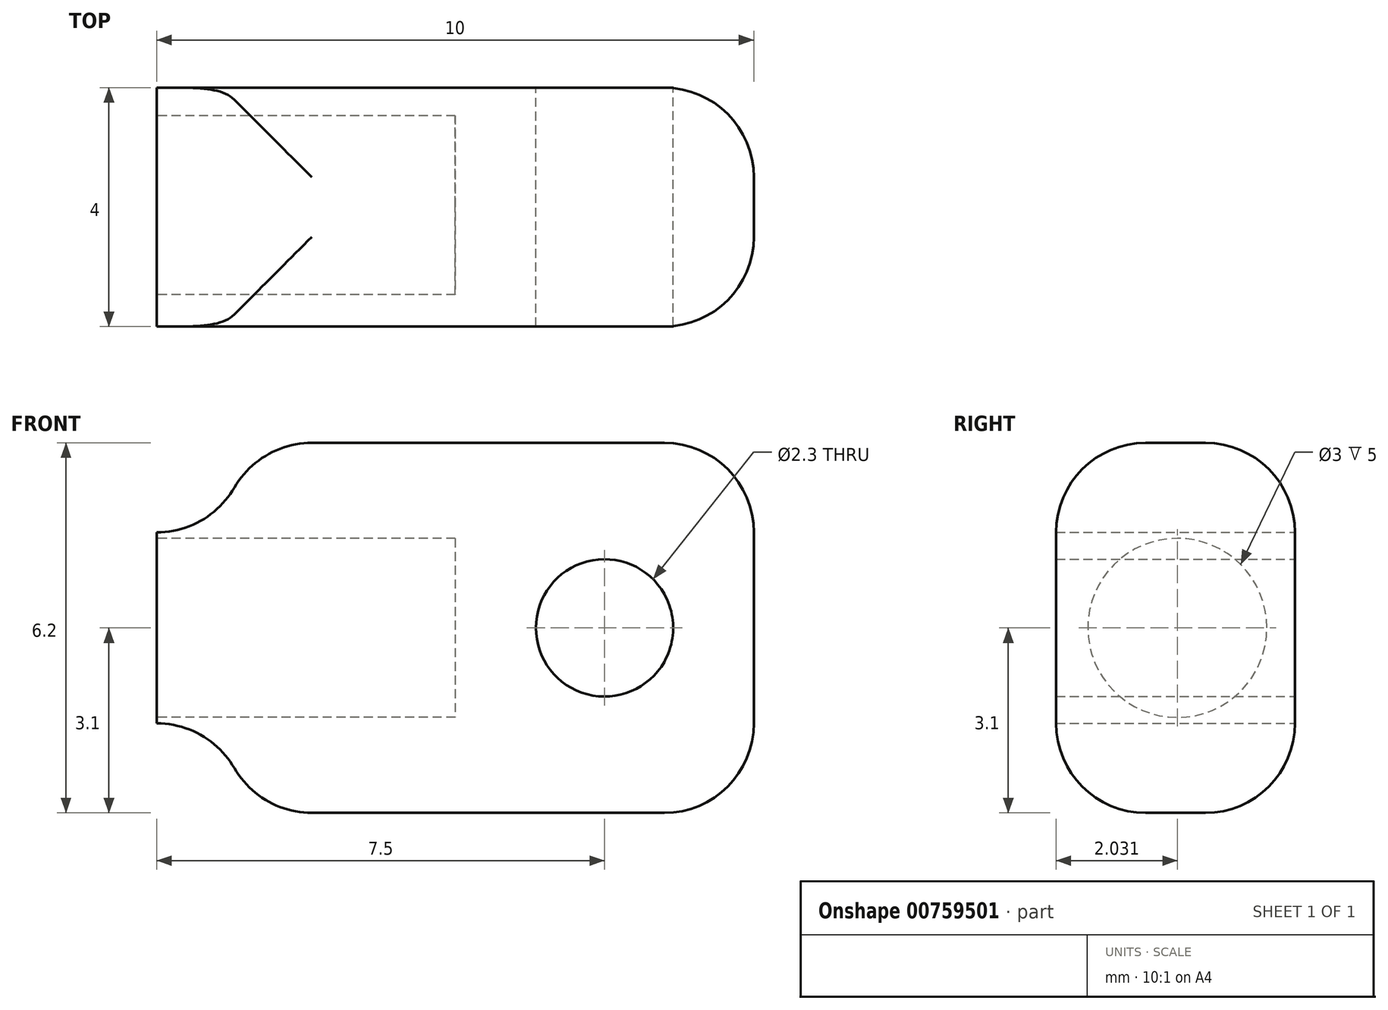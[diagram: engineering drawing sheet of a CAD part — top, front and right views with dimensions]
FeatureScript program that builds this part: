
annotation { "Feature Type Name" : "Feature", "Feature Type Description" : "" }
export const myFeature = defineFeature(function(context is Context, id is Id, definition is map)
    precondition{}
    {
        {
            var Q0;
            Q0=qCreatedBy(makeId("Front.planeOp"),FACE);
            var sketch = newSketch(context, id + "F0", { "sketchPlane" : qUnion([Q0])});
            skLineSegment(sketch, "E0.bottom", {"start": v(-3.5, 3.1) * mm, "end": v(5, 3.1) * mm});
            skLineSegment(sketch, "E0.top", {"start": v(-3.5, -3.1) * mm, "end": v(5, -3.1) * mm});
            skLineSegment(sketch, "E0.left", {"start": v(-5, 1.6) * mm, "end": v(-5, -1.6) * mm});
            skLineSegment(sketch, "E0.right", {"start": v(5, 3.1) * mm, "end": v(5, -3.1) * mm});
            skPoint(sketch, "E0.middle", {"position": v(0, 0) * mm});
            skCircle(sketch, "E1", {"center": v(2.5, 0) * mm, "radius": 1.15 * mm});
            skArc(sketch, "E2", {"start": v(-3.5, 3.1) * mm, "mid": v(-3.94, 2.04) * mm, "end": v(-5, 1.6) * mm});
            skArc(sketch, "E3.MirrorCS", {"start": v(-3.5, -3.1) * mm, "mid": v(-3.94, -2.04) * mm, "end": v(-5, -1.6) * mm});
            skSolve(sketch);
        }
        {
            var Q0;
            Q0 = qSketchRegion(id + "F0", true);
            extrude(context, id + "F1", {"entities" : qUnion([Q0]), "depth" : 4 * mm, "offsetDistance" : 25 * mm});
        }
        {
            var Q0;
            Q0=makeQuery(id+"F1.opExtrude","SWEPT_FACE",FACE,{"disambiguationData":[OSD([sQuery(id+"F0.wireOp",EDGE,"E0.left")])]});
            var sketch = newSketch(context, id + "F2", { "sketchPlane" : qUnion([Q0])});
            skCircle(sketch, "E4", {"center": v(1.97, 0) * mm, "radius": 1.5 * mm});
            skSolve(sketch);
        }
        {
            var Q0;
            Q0 = qSketchRegion(id + "F2", true);
            extrude(context, id + "F3", {"entities" : qUnion([Q0]), "operationType" : NewBodyOperationType.REMOVE, "oppositeDirection" : true, "depth" : 5 * mm, "offsetDistance" : 25 * mm});
        }
        {
            var Q0;
            Q0=makeQuery(id+"F1.opExtrude","SWEPT_EDGE",EDGE,{"disambiguationData":[OSD([sQuery(id+"F0.wireOp",EDGE,"E0.bottom"),sQuery(id+"F0.wireOp",EDGE,"E2")])]});
            var Q1;
            Q1=makeQuery(id+"F1.opExtrude","SWEPT_EDGE",EDGE,{"disambiguationData":[OSD([sQuery(id+"F0.wireOp",EDGE,"E0.top"),sQuery(id+"F0.wireOp",EDGE,"E3.MirrorCS")])]});
            var Q2;
            Q2=makeQuery(id+"F1.opExtrude","SWEPT_EDGE",EDGE,{"disambiguationData":[OSD([sQuery(id+"F0.wireOp",EDGE,"E0.bottom"),sQuery(id+"F0.wireOp",EDGE,"E0.right")])]});
            var Q3;
            Q3=makeQuery(id+"F1.opExtrude","CAP_EDGE",EDGE,{"disambiguationData":[OSD([sQuery(id+"F0.wireOp",EDGE,"E0.bottom")])],"isStart":false});
            var Q4;
            Q4=makeQuery(id+"F1.opExtrude","CAP_EDGE",EDGE,{"disambiguationData":[OSD([sQuery(id+"F0.wireOp",EDGE,"E0.bottom")])],"isStart":true});
            var Q5;
            Q5=makeQuery(id+"F1.opExtrude","CAP_EDGE",EDGE,{"disambiguationData":[OSD([sQuery(id+"F0.wireOp",EDGE,"E0.top")])],"isStart":true});
            var Q6;
            Q6=makeQuery(id+"F1.opExtrude","SWEPT_FACE",FACE,{"disambiguationData":[OSD([sQuery(id+"F0.wireOp",EDGE,"E0.right")])]});
            var Q7;
            Q7=makeQuery(id+"F1.opExtrude","CAP_EDGE",EDGE,{"disambiguationData":[OSD([sQuery(id+"F0.wireOp",EDGE,"E0.top")])],"isStart":false});
            fillet(context, id + "F4", {"entities" : qUnion([Q0, Q1, Q2, Q3, Q4, Q5, Q6, Q7]), "radius" : 1.5 * mm, "tangentPropagation" : true, "allowEdgeOverflow" : false});
        }
    });
